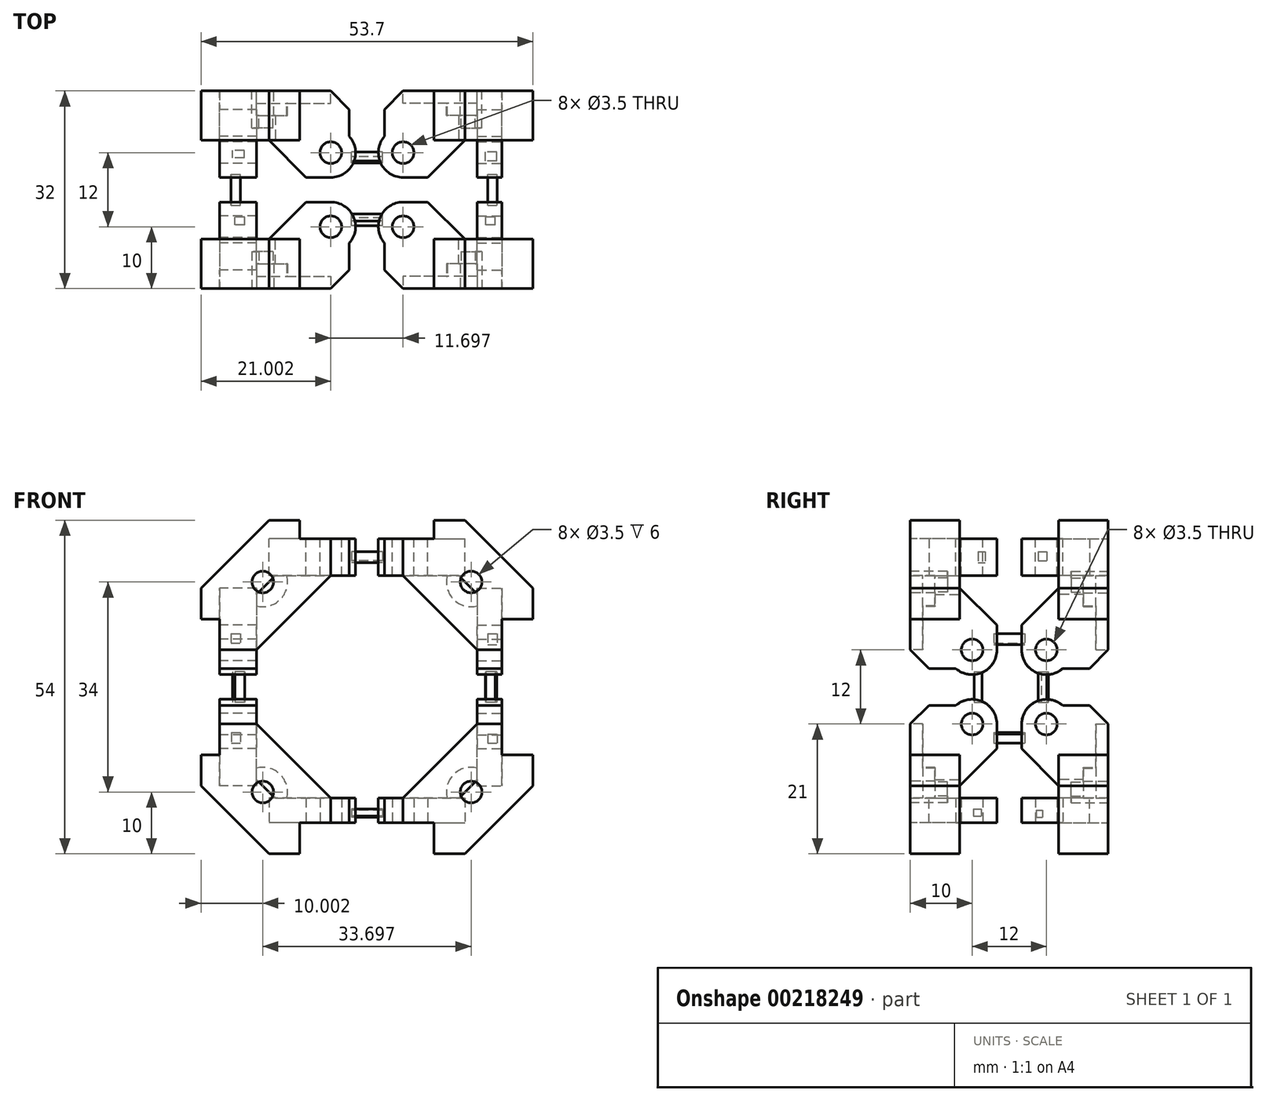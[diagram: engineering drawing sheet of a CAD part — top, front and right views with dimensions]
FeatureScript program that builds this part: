
annotation { "Feature Type Name" : "Feature", "Feature Type Description" : "" }
export const myFeature = defineFeature(function(context is Context, id is Id, definition is map)
    precondition{}
    {
        {
            var Q0;
            Q0=qCreatedBy(makeId("Top.planeOp"),FACE);
            cPlane(context, id + "F0", {"entities" : qUnion([Q0]), "cplaneType" : CPlaneType.OFFSET, "offset" : 18 * mm, "width" : 150 * mm, "height" : 150 * mm});
        }
        {
            var Q0;
            Q0=qCreatedBy(makeId("Front.planeOp"),FACE);
            var sketch = newSketch(context, id + "F1", { "sketchPlane" : qUnion([Q0])});
            skLineSegment(sketch, "E0", {"start": v(14.85, 0) * mm, "end": v(17.85, 0) * mm, "construction": true});
            skLineSegment(sketch, "E1", {"start": v(17.85, 0) * mm, "end": v(17.85, 3) * mm, "construction": true});
            skLineSegment(sketch, "E2", {"start": v(14.85, 0) * mm, "end": v(17.85, 3) * mm});
            skLineSegment(sketch, "E3", {"start": v(14.85, 0) * mm, "end": v(10.85, 0) * mm});
            skLineSegment(sketch, "E4", {"start": v(10.85, 0) * mm, "end": v(10.85, -9) * mm});
            skLineSegment(sketch, "E5", {"start": v(10.85, -9) * mm, "end": v(15.85, -9) * mm});
            skLineSegment(sketch, "E6", {"start": v(17.85, 3) * mm, "end": v(17.85, 7) * mm});
            skLineSegment(sketch, "E7", {"start": v(17.85, 7) * mm, "end": v(26.85, 7) * mm});
            skLineSegment(sketch, "E8", {"start": v(26.85, 7) * mm, "end": v(26.85, 2) * mm});
            skLineSegment(sketch, "E9", {"start": v(26.85, 2) * mm, "end": v(15.85, -9) * mm});
            skLineSegment(sketch, "E10", {"start": v(15.85, -9) * mm, "end": v(26.85, -9) * mm, "construction": true});
            skLineSegment(sketch, "E11", {"start": v(26.85, -9) * mm, "end": v(26.85, 2) * mm, "construction": true});
            skSolve(sketch);
        }
        {
            var Q0;
            Q0=makeQuery(id+"F1.imprint","IMPRINT",FACE,{"disambiguationData":[TD([[makeQuery(id+"F1.imprint","IMPRINT",EDGE,{"derivedFrom":sQuery(id+"F1.wireOp",EDGE,"E2")}),-1.0]])]});
            extrude(context, id + "F2", {"entities" : qUnion([Q0]), "depth" : 8 * mm});
        }
        {
            var Q0;
            Q0=makeQuery(id+"F2.opExtrude","CAP_FACE",FACE,{"disambiguationData":[OSD([sQuery(id+"F1.wireOp",EDGE,"E2"),sQuery(id+"F1.wireOp",EDGE,"E3"),sQuery(id+"F1.wireOp",EDGE,"E4"),sQuery(id+"F1.wireOp",EDGE,"E5"),sQuery(id+"F1.wireOp",EDGE,"E6"),sQuery(id+"F1.wireOp",EDGE,"E7"),sQuery(id+"F1.wireOp",EDGE,"E8"),sQuery(id+"F1.wireOp",EDGE,"E9")])],"isStart":false});
            var sketch = newSketch(context, id + "F3", { "sketchPlane" : qUnion([Q0])});
            skLineSegment(sketch, "E12", {"start": v(26.85, -9) * mm, "end": v(26.85, 2) * mm, "construction": true});
            skLineSegment(sketch, "E13", {"start": v(26.85, 1) * mm, "end": v(16.85, 1) * mm, "construction": true});
            skCircle(sketch, "E14", {"center": v(16.85, 1) * mm, "radius": 1.75 * mm});
            skCircle(sketch, "E15", {"center": v(16.85, 1) * mm, "radius": 4 * mm});
            skLineSegment(sketch, "E16", {"start": v(26.85, -9) * mm, "end": v(15.85, -9) * mm, "construction": true});
            skSolve(sketch);
        }
        {
            var Q0;
            {var subQ0=sQuery(id+"F3.wireOp",EDGE,"xhRyTsUT-o3e5-bvfq-njYf-te9PrhzOYERQ");Q0=makeQuery(id+"F3.imprint","IMPRINT",FACE,{"disambiguationData":[TD([[makeQuery(id+"F3.imprint","IMPRINT",EDGE,{"derivedFrom":subQ0}),-1.0]])]});}
            var Q1;
            Q1=makeQuery(id+"F3.imprint","IMPRINT",FACE,{"disambiguationData":[TD([[makeQuery(id+"F3.imprint","IMPRINT",EDGE,{"derivedFrom":sQuery(id+"F3.wireOp",EDGE,"E14")}),-1.0]])]});
            var Q2;
            {var subQ0=sQuery(id+"F3.wireOp",EDGE,"xAzglln9-Erma-ZddH-ddn6-ssYke3hLXc0D");Q2=makeQuery(id+"F3.imprint","IMPRINT",FACE,{"disambiguationData":[TD([[makeQuery(id+"F3.imprint","IMPRINT",EDGE,{"derivedFrom":subQ0}),1.0]])]});}
            extrude(context, id + "F4", {"entities" : qUnion([Q0, Q1, Q2]), "operationType" : NewBodyOperationType.ADD, "oppositeDirection" : true, "depth" : 4 * mm});
        }
        {
            var Q0;
            Q0=makeQuery(id+"F2.opExtrude","SWEPT_FACE",FACE,{"disambiguationData":[OSD([sQuery(id+"F1.wireOp",EDGE,"E7")])]});
            var sketch = newSketch(context, id + "F5", { "sketchPlane" : qUnion([Q0])});
            skLineSegment(sketch, "E17", {"start": v(21.85, 0) * mm, "end": v(21.85, -8) * mm});
            skLineSegment(sketch, "E18", {"start": v(21.85, 0) * mm, "end": v(17.85, 0) * mm});
            skLineSegment(sketch, "E19", {"start": v(17.85, 0) * mm, "end": v(17.85, -8) * mm});
            skLineSegment(sketch, "E20", {"start": v(17.85, -8) * mm, "end": v(21.85, -8) * mm});
            skSolve(sketch);
        }
        {
            var Q0;
            Q0=makeQuery(id+"F5.imprint","IMPRINT",FACE,{"disambiguationData":[TD([[makeQuery(id+"F5.imprint","IMPRINT",EDGE,{"derivedFrom":sQuery(id+"F5.wireOp",EDGE,"E17")}),-1.0]])]});
            extrude(context, id + "F6", {"entities" : qUnion([Q0]), "operationType" : NewBodyOperationType.ADD, "depth" : 8 * mm});
        }
        {
            var Q0;
            {var subQ0=sQuery(id+"F3.wireOp",EDGE,"E14");var subQ1=makeQuery(id+"F2.opExtrude","CAP_EDGE",EDGE,{"disambiguationData":[OSD([sQuery(id+"F1.wireOp",EDGE,"E2")])],"isStart":false});var subQ2=makeQuery(id+"F3.imprint","INTERSECT",VERTEX,{"disambiguationData":[OD(0.0)],"derivedFrom":[subQ1,subQ0]});Q0=makeQuery(id+"F3.imprint","IMPRINT",FACE,{"disambiguationData":[TD([[makeQuery(id+"F3.imprint","IMPRINT",EDGE,{"disambiguationData":[TD([[subQ2,-1.0]])],"derivedFrom":subQ0}),1.0]])]});}
            extrude(context, id + "F7", {"entities" : qUnion([Q0]), "operationType" : NewBodyOperationType.REMOVE, "oppositeDirection" : true, "depth" : 6 * mm});
        }
        {
            var Q0;
            Q0=makeQuery(id+"F6.opExtrude","SWEPT_FACE",FACE,{"disambiguationData":[OSD([sQuery(id+"F5.wireOp",EDGE,"E17")])]});
            var sketch = newSketch(context, id + "F8", { "sketchPlane" : qUnion([Q0])});
            skLineSegment(sketch, "E21", {"start": v(-8, 12) * mm, "end": v(2, 12) * mm, "construction": true});
            skCircle(sketch, "E22", {"center": v(2, 12) * mm, "radius": 1.75 * mm});
            skCircle(sketch, "E23", {"center": v(2, 12) * mm, "radius": 4 * mm});
            skLineSegment(sketch, "E24", {"start": v(0, 7) * mm, "end": v(0, 2) * mm});
            skLineSegment(sketch, "E25", {"start": v(0, 2) * mm, "end": v(6, 8) * mm});
            skLineSegment(sketch, "E26", {"start": v(2, 12) * mm, "end": v(6, 12) * mm, "construction": true});
            skLineSegment(sketch, "E27", {"start": v(6, 12) * mm, "end": v(6, 8) * mm});
            skSolve(sketch);
        }
        {
            var Q0;
            Q0=qSketchRegion(id+"F8",true);
            var Q1;
            {var subQ0=sQuery(id+"F8.wireOp",EDGE,"GLTiPWO5-g4RS-G08f-K7BW-j4bQh8QSFt7y");Q1=makeQuery(id+"F8.imprint","IMPRINT",FACE,{"disambiguationData":[TD([[makeQuery(id+"F8.imprint","IMPRINT",EDGE,{"derivedFrom":subQ0}),1.0]])]});}
            var Q2;
            {var subQ1=sQuery(id+"F8.wireOp",EDGE,"E24");Q2=makeQuery(id+"F8.imprint","IMPRINT",FACE,{"disambiguationData":[TD([[makeQuery(id+"F8.imprint","IMPRINT",EDGE,{"derivedFrom":subQ1}),1.0]])]});}
            extrude(context, id + "F9", {"entities" : qUnion([Q0, Q1, Q2]), "operationType" : NewBodyOperationType.ADD, "oppositeDirection" : true, "depth" : 4 * mm});
        }
        {
            var Q0;
            Q0=makeQuery(id+"F2.opExtrude","SWEPT_FACE",FACE,{"disambiguationData":[OSD([sQuery(id+"F1.wireOp",EDGE,"E4")])]});
            var sketch = newSketch(context, id + "F10", { "sketchPlane" : qUnion([Q0])});
            skLineSegment(sketch, "E28.bottom", {"start": v(0, 0) * mm, "end": v(8, 0) * mm});
            skLineSegment(sketch, "E28.top", {"start": v(0, -4) * mm, "end": v(8, -4) * mm});
            skLineSegment(sketch, "E28.left", {"start": v(0, 0) * mm, "end": v(0, -4) * mm});
            skLineSegment(sketch, "E28.right", {"start": v(8, 0) * mm, "end": v(8, -4) * mm});
            skSolve(sketch);
        }
        {
            var Q0;
            Q0=makeQuery(id+"F10.imprint","IMPRINT",FACE,{"disambiguationData":[TD([[makeQuery(id+"F10.imprint","IMPRINT",EDGE,{"derivedFrom":sQuery(id+"F10.wireOp",EDGE,"E28.bottom")}),1.0]])]});
            extrude(context, id + "F11", {"entities" : qUnion([Q0]), "operationType" : NewBodyOperationType.ADD, "depth" : 8 * mm});
        }
        {
            var Q0;
            Q0=makeQuery(id+"F11.opExtrude","SWEPT_FACE",FACE,{"disambiguationData":[OSD([sQuery(id+"F10.wireOp",EDGE,"E28.top")])]});
            var sketch = newSketch(context, id + "F12", { "sketchPlane" : qUnion([Q0])});
            skLineSegment(sketch, "E29", {"start": v(5.85, 8) * mm, "end": v(5.85, -2) * mm, "construction": true});
            skCircle(sketch, "E30", {"center": v(5.85, -2) * mm, "radius": 1.75 * mm});
            skCircle(sketch, "E31", {"center": v(5.85, -2) * mm, "radius": 4 * mm});
            skLineSegment(sketch, "E32", {"start": v(10.85, 0) * mm, "end": v(15.85, 0) * mm});
            skLineSegment(sketch, "E33", {"start": v(5.85, -2) * mm, "end": v(5.85, -6) * mm, "construction": true});
            skLineSegment(sketch, "E34", {"start": v(5.85, -6) * mm, "end": v(9.85, -6) * mm});
            skLineSegment(sketch, "E35", {"start": v(9.85, -6) * mm, "end": v(15.85, 0) * mm});
            skSolve(sketch);
        }
        {
            var Q0;
            Q0=makeQuery(id+"F12.imprint","IMPRINT",FACE,{"disambiguationData":[TD([[makeQuery(id+"F12.imprint","IMPRINT",EDGE,{"derivedFrom":sQuery(id+"F12.wireOp",EDGE,"E30")}),-1.0]])]});
            var Q1;
            {var subQ0=sQuery(id+"F12.wireOp",EDGE,"zv0TR8YQ-G6ir-l7lB-xXnJ-DlvVZtNBSlEO");Q1=makeQuery(id+"F12.imprint","IMPRINT",FACE,{"disambiguationData":[TD([[makeQuery(id+"F12.imprint","IMPRINT",EDGE,{"derivedFrom":subQ0}),-1.0]])]});}
            var Q2;
            {var subQ1=sQuery(id+"F12.wireOp",EDGE,"E32");Q2=makeQuery(id+"F12.imprint","IMPRINT",FACE,{"disambiguationData":[TD([[makeQuery(id+"F12.imprint","IMPRINT",EDGE,{"derivedFrom":subQ1}),-1.0]])]});}
            extrude(context, id + "F13", {"entities" : qUnion([Q0, Q1, Q2]), "operationType" : NewBodyOperationType.ADD, "oppositeDirection" : true, "depth" : 4 * mm});
        }
        {
            var Q0;
            Q0=makeQuery(id+"F11.opExtrude","CAP_EDGE",EDGE,{"disambiguationData":[OSD([sQuery(id+"F10.wireOp",EDGE,"E28.right")])],"isStart":false});
            var Q1;
            Q1=makeQuery(id+"F6.opExtrude","CAP_EDGE",EDGE,{"disambiguationData":[OSD([sQuery(id+"F5.wireOp",EDGE,"E20")])],"isStart":false});
            chamfer(context, id + "F14", {"entities" : qUnion([Q0, Q1]), "width" : 3 * mm, "tangentPropagation" : true});
        }
        {
            var Q0;
            Q0=makeQuery(id+"F11.boolean.opBoolean","MERGE",FACE,{"derivedFrom":[makeQuery(id+"F6.boolean.opBoolean","MERGE",FACE,{"derivedFrom":[makeQuery(id+"F4.boolean.opBoolean","MERGE",FACE,{"derivedFrom":[makeQuery(id+"F2.opExtrude","CAP_FACE",FACE,{"disambiguationData":[OSD([sQuery(id+"F1.wireOp",EDGE,"E2"),sQuery(id+"F1.wireOp",EDGE,"E3"),sQuery(id+"F1.wireOp",EDGE,"E4"),sQuery(id+"F1.wireOp",EDGE,"E5"),sQuery(id+"F1.wireOp",EDGE,"E6"),sQuery(id+"F1.wireOp",EDGE,"E7"),sQuery(id+"F1.wireOp",EDGE,"E8"),sQuery(id+"F1.wireOp",EDGE,"E9")])],"isStart":false}),makeQuery(id+"F4.opExtrude","CAP_FACE",FACE,{"disambiguationData":[OSD([sQuery(id+"F3.wireOp",EDGE,"E14"),sQuery(id+"F3.wireOp",EDGE,"E15")])],"isStart":true})]}),makeQuery(id+"F6.opExtrude","SWEPT_FACE",FACE,{"disambiguationData":[OSD([sQuery(id+"F5.wireOp",EDGE,"E20")])]})]}),makeQuery(id+"F11.opExtrude","SWEPT_FACE",FACE,{"disambiguationData":[OSD([sQuery(id+"F10.wireOp",EDGE,"E28.right")])]})]});
            var sketch = newSketch(context, id + "F15", { "sketchPlane" : qUnion([Q0])});
            skLineSegment(sketch, "E36", {"start": v(17.85, 12) * mm, "end": v(5.85, 0) * mm});
            skSolve(sketch);
        }
        {
            var Q0;
            Q0=makeQuery(id+"F15.imprint","IMPRINT",FACE,{"disambiguationData":[TD([[makeQuery(id+"F15.imprint","IMPRINT",EDGE,{"derivedFrom":sQuery(id+"F15.wireOp",EDGE,"E36")}),1.0]])]});
            extrude(context, id + "F16", {"entities" : qUnion([Q0]), "operationType" : NewBodyOperationType.ADD, "oppositeDirection" : true, "depth" : 2 * mm});
        }
        {
            var Q0;
            Q0=makeQuery(id+"F2.opExtrude","SWEPT_BODY",BODY,{"disambiguationData":[OSD([sQuery(id+"F1.wireOp",EDGE,"E2"),sQuery(id+"F1.wireOp",EDGE,"E3"),sQuery(id+"F1.wireOp",EDGE,"E4"),sQuery(id+"F1.wireOp",EDGE,"E5"),sQuery(id+"F1.wireOp",EDGE,"E6"),sQuery(id+"F1.wireOp",EDGE,"E7"),sQuery(id+"F1.wireOp",EDGE,"E8"),sQuery(id+"F1.wireOp",EDGE,"E9")])]});
            var Q1;
            Q1=qCreatedBy(makeId("Right.planeOp"),FACE);
            mirror(context, id + "F17", {"entities" : qUnion([Q0]), "mirrorPlane" : qUnion([Q1])});
        }
        {
            var Q0;
            {var subQ0=sQuery(id+"F5.wireOp",EDGE,"E17");Q0=makeQuery(id+"F17.opPattern","COPY",FACE,{"derivedFrom":makeQuery(id+"F9.boolean.opBoolean","MERGE",FACE,{"derivedFrom":[makeQuery(id+"F6.opExtrude","SWEPT_FACE",FACE,{"disambiguationData":[OSD([subQ0])]}),makeQuery(id+"F9.opExtrude","CAP_FACE",FACE,{"disambiguationData":[OSD([sQuery(id+"F1.wireOp",EDGE,"E7"),subQ0,sQuery(id+"F5.wireOp",EDGE,"E18"),sQuery(id+"F8.wireOp",EDGE,"E22"),sQuery(id+"F8.wireOp",EDGE,"E23"),sQuery(id+"F8.wireOp",EDGE,"E24"),sQuery(id+"F8.wireOp",EDGE,"E25"),sQuery(id+"F8.wireOp",EDGE,"E27")])],"isStart":true})]}),"instanceName":"1"});}
            extrude(context, id + "F18", {"entities" : qUnion([Q0]), "operationType" : NewBodyOperationType.ADD, "depth" : 2 * mm});
        }
        {
            var Q0;
            Q0=makeQuery(id+"F17.opPattern","COPY",BODY,{"derivedFrom":makeQuery(id+"F2.opExtrude","SWEPT_BODY",BODY,{"disambiguationData":[OSD([sQuery(id+"F1.wireOp",EDGE,"E2"),sQuery(id+"F1.wireOp",EDGE,"E3"),sQuery(id+"F1.wireOp",EDGE,"E4"),sQuery(id+"F1.wireOp",EDGE,"E5"),sQuery(id+"F1.wireOp",EDGE,"E6"),sQuery(id+"F1.wireOp",EDGE,"E7"),sQuery(id+"F1.wireOp",EDGE,"E8"),sQuery(id+"F1.wireOp",EDGE,"E9")])]}),"instanceName":"1"});
            var Q1;
            Q1=qCreatedBy(id+"F0.planeOp",FACE);
            mirror(context, id + "F19", {"entities" : qUnion([Q0]), "mirrorPlane" : qUnion([Q1])});
        }
        {
            var Q0;
            {var subQ0=sQuery(id+"F10.wireOp",EDGE,"E28.top");Q0=makeQuery(id+"F19.opPattern","COPY",FACE,{"derivedFrom":makeQuery(id+"F17.opPattern","COPY",FACE,{"derivedFrom":makeQuery(id+"F13.boolean.opBoolean","MERGE",FACE,{"derivedFrom":[makeQuery(id+"F11.opExtrude","SWEPT_FACE",FACE,{"disambiguationData":[OSD([subQ0])]}),makeQuery(id+"F13.opExtrude","CAP_FACE",FACE,{"disambiguationData":[OSD([sQuery(id+"F1.wireOp",EDGE,"E4"),subQ0,sQuery(id+"F10.wireOp",EDGE,"E28.left"),sQuery(id+"F12.wireOp",EDGE,"E30"),sQuery(id+"F12.wireOp",EDGE,"E31"),sQuery(id+"F12.wireOp",EDGE,"E32"),sQuery(id+"F12.wireOp",EDGE,"E34"),sQuery(id+"F12.wireOp",EDGE,"E35")])],"isStart":true})]}),"instanceName":"1"}),"instanceName":"1"});}
            extrude(context, id + "F20", {"entities" : qUnion([Q0]), "operationType" : NewBodyOperationType.ADD, "depth" : 2 * mm});
        }
        {
            var Q0;
            Q0=qCreatedBy(makeId("Front.planeOp"),FACE);
            cPlane(context, id + "F21", {"entities" : qUnion([Q0]), "cplaneType" : CPlaneType.OFFSET, "offset" : 8 * mm, "oppositeDirection" : true, "width" : 150 * mm, "height" : 150 * mm});
        }
        {
            var Q0;
            Q0=makeQuery(id+"F17.opPattern","COPY",BODY,{"derivedFrom":makeQuery(id+"F2.opExtrude","SWEPT_BODY",BODY,{"disambiguationData":[OSD([sQuery(id+"F1.wireOp",EDGE,"E2"),sQuery(id+"F1.wireOp",EDGE,"E3"),sQuery(id+"F1.wireOp",EDGE,"E4"),sQuery(id+"F1.wireOp",EDGE,"E5"),sQuery(id+"F1.wireOp",EDGE,"E6"),sQuery(id+"F1.wireOp",EDGE,"E7"),sQuery(id+"F1.wireOp",EDGE,"E8"),sQuery(id+"F1.wireOp",EDGE,"E9")])]}),"instanceName":"1"});
            var Q1;
            Q1=makeQuery(id+"F19.opPattern","COPY",BODY,{"derivedFrom":makeQuery(id+"F17.opPattern","COPY",BODY,{"derivedFrom":makeQuery(id+"F2.opExtrude","SWEPT_BODY",BODY,{"disambiguationData":[OSD([sQuery(id+"F1.wireOp",EDGE,"E2"),sQuery(id+"F1.wireOp",EDGE,"E3"),sQuery(id+"F1.wireOp",EDGE,"E4"),sQuery(id+"F1.wireOp",EDGE,"E5"),sQuery(id+"F1.wireOp",EDGE,"E6"),sQuery(id+"F1.wireOp",EDGE,"E7"),sQuery(id+"F1.wireOp",EDGE,"E8"),sQuery(id+"F1.wireOp",EDGE,"E9")])]}),"instanceName":"1"}),"instanceName":"1"});
            var Q2;
            Q2=qCreatedBy(id+"F21.planeOp",FACE);
            mirror(context, id + "F22", {"entities" : qUnion([Q0, Q1]), "mirrorPlane" : qUnion([Q2])});
        }
        {
            var Q0;
            Q0=makeQuery(id+"F2.opExtrude","SWEPT_BODY",BODY,{"disambiguationData":[OSD([sQuery(id+"F1.wireOp",EDGE,"E2"),sQuery(id+"F1.wireOp",EDGE,"E3"),sQuery(id+"F1.wireOp",EDGE,"E4"),sQuery(id+"F1.wireOp",EDGE,"E5"),sQuery(id+"F1.wireOp",EDGE,"E6"),sQuery(id+"F1.wireOp",EDGE,"E7"),sQuery(id+"F1.wireOp",EDGE,"E8"),sQuery(id+"F1.wireOp",EDGE,"E9")])]});
            var Q1;
            Q1=qCreatedBy(id+"F21.planeOp",FACE);
            mirror(context, id + "F23", {"entities" : qUnion([Q0]), "mirrorPlane" : qUnion([Q1])});
        }
        {
            var Q0;
            Q0=makeQuery(id+"F2.opExtrude","SWEPT_BODY",BODY,{"disambiguationData":[OSD([sQuery(id+"F1.wireOp",EDGE,"E2"),sQuery(id+"F1.wireOp",EDGE,"E3"),sQuery(id+"F1.wireOp",EDGE,"E4"),sQuery(id+"F1.wireOp",EDGE,"E5"),sQuery(id+"F1.wireOp",EDGE,"E6"),sQuery(id+"F1.wireOp",EDGE,"E7"),sQuery(id+"F1.wireOp",EDGE,"E8"),sQuery(id+"F1.wireOp",EDGE,"E9")])]});
            var Q1;
            Q1=makeQuery(id+"F23.opPattern","COPY",BODY,{"derivedFrom":makeQuery(id+"F2.opExtrude","SWEPT_BODY",BODY,{"disambiguationData":[OSD([sQuery(id+"F1.wireOp",EDGE,"E2"),sQuery(id+"F1.wireOp",EDGE,"E3"),sQuery(id+"F1.wireOp",EDGE,"E4"),sQuery(id+"F1.wireOp",EDGE,"E5"),sQuery(id+"F1.wireOp",EDGE,"E6"),sQuery(id+"F1.wireOp",EDGE,"E7"),sQuery(id+"F1.wireOp",EDGE,"E8"),sQuery(id+"F1.wireOp",EDGE,"E9")])]}),"instanceName":"1"});
            var Q2;
            Q2=qCreatedBy(id+"F0.planeOp",FACE);
            mirror(context, id + "F24", {"entities" : qUnion([Q0, Q1]), "mirrorPlane" : qUnion([Q2])});
        }
        {
            var Q0;
            {var subQ0=sQuery(id+"F10.wireOp",EDGE,"E28.top");Q0=makeQuery(id+"F24.opPattern","COPY",FACE,{"derivedFrom":makeQuery(id+"F13.boolean.opBoolean","MERGE",FACE,{"derivedFrom":[makeQuery(id+"F11.opExtrude","SWEPT_FACE",FACE,{"disambiguationData":[OSD([subQ0])]}),makeQuery(id+"F13.opExtrude","CAP_FACE",FACE,{"disambiguationData":[OSD([sQuery(id+"F1.wireOp",EDGE,"E4"),subQ0,sQuery(id+"F10.wireOp",EDGE,"E28.left"),sQuery(id+"F12.wireOp",EDGE,"E30"),sQuery(id+"F12.wireOp",EDGE,"E31"),sQuery(id+"F12.wireOp",EDGE,"E32"),sQuery(id+"F12.wireOp",EDGE,"E34"),sQuery(id+"F12.wireOp",EDGE,"E35")])],"isStart":true})]}),"instanceName":"1"});}
            var Q1;
            {var subQ0=sQuery(id+"F10.wireOp",EDGE,"E28.top");Q1=makeQuery(id+"F24.opPattern","COPY",FACE,{"derivedFrom":makeQuery(id+"F23.opPattern","COPY",FACE,{"derivedFrom":makeQuery(id+"F13.boolean.opBoolean","MERGE",FACE,{"derivedFrom":[makeQuery(id+"F11.opExtrude","SWEPT_FACE",FACE,{"disambiguationData":[OSD([subQ0])]}),makeQuery(id+"F13.opExtrude","CAP_FACE",FACE,{"disambiguationData":[OSD([sQuery(id+"F1.wireOp",EDGE,"E4"),subQ0,sQuery(id+"F10.wireOp",EDGE,"E28.left"),sQuery(id+"F12.wireOp",EDGE,"E30"),sQuery(id+"F12.wireOp",EDGE,"E31"),sQuery(id+"F12.wireOp",EDGE,"E32"),sQuery(id+"F12.wireOp",EDGE,"E34"),sQuery(id+"F12.wireOp",EDGE,"E35")])],"isStart":true})]}),"instanceName":"1"}),"instanceName":"1"});}
            extrude(context, id + "F25", {"entities" : qUnion([Q0, Q1]), "operationType" : NewBodyOperationType.ADD, "depth" : 2 * mm});
        }
        {
            var Q0;
            Q0=qCreatedBy(id+"F21.planeOp",FACE);
            var sketch = newSketch(context, id + "F26", { "sketchPlane" : qUnion([Q0])});
            skLineSegment(sketch, "E37.bottom", {"start": v(-22.03, 26.65) * mm, "end": v(-20.49, 26.65) * mm});
            skLineSegment(sketch, "E37.top", {"start": v(-22.03, 25.11) * mm, "end": v(-20.49, 25.11) * mm});
            skLineSegment(sketch, "E37.left", {"start": v(-22.03, 26.65) * mm, "end": v(-22.03, 25.11) * mm});
            skLineSegment(sketch, "E37.right", {"start": v(-20.49, 26.65) * mm, "end": v(-20.49, 25.11) * mm});
            skLineSegment(sketch, "E38.bottom", {"start": v(-21.94, 10.62) * mm, "end": v(-20.49, 10.62) * mm});
            skLineSegment(sketch, "E38.top", {"start": v(-21.94, 8.92) * mm, "end": v(-20.49, 8.92) * mm});
            skLineSegment(sketch, "E38.left", {"start": v(-21.94, 10.62) * mm, "end": v(-21.94, 8.92) * mm});
            skLineSegment(sketch, "E38.right", {"start": v(-20.49, 10.62) * mm, "end": v(-20.49, 8.92) * mm});
            skLineSegment(sketch, "E39.bottom", {"start": v(19.51, 10.38) * mm, "end": v(21.05, 10.38) * mm});
            skLineSegment(sketch, "E39.top", {"start": v(19.51, 8.92) * mm, "end": v(21.05, 8.92) * mm});
            skLineSegment(sketch, "E39.left", {"start": v(19.51, 10.38) * mm, "end": v(19.51, 8.92) * mm});
            skLineSegment(sketch, "E39.right", {"start": v(21.05, 10.38) * mm, "end": v(21.05, 8.92) * mm});
            skLineSegment(sketch, "E40.bottom", {"start": v(19.51, 26.65) * mm, "end": v(21.05, 26.65) * mm});
            skLineSegment(sketch, "E40.top", {"start": v(19.51, 24.87) * mm, "end": v(21.05, 24.87) * mm});
            skLineSegment(sketch, "E40.left", {"start": v(19.51, 26.65) * mm, "end": v(19.51, 24.87) * mm});
            skLineSegment(sketch, "E40.right", {"start": v(21.05, 26.65) * mm, "end": v(21.05, 24.87) * mm});
            skLineSegment(sketch, "E41", {"start": v(-20.49, 26.65) * mm, "end": v(19.51, 26.65) * mm, "construction": true});
            skLineSegment(sketch, "E42", {"start": v(-20.49, 8.92) * mm, "end": v(19.51, 8.92) * mm, "construction": true});
            skSolve(sketch);
        }
        {
            var Q0;
            Q0=qSketchRegion(id+"F26",true);
            extrude(context, id + "F27", {"entities" : qUnion([Q0]), "endBound" : BoundingType.SYMMETRIC, "depth" : 5 * mm});
        }
        {
            var Q0;
            Q0=qCreatedBy(id+"F0.planeOp",FACE);
            var sketch = newSketch(context, id + "F28", { "sketchPlane" : qUnion([Q0])});
            skLineSegment(sketch, "E43.bottom", {"start": v(20.73, 2.3) * mm, "end": v(19.21, 2.3) * mm});
            skLineSegment(sketch, "E43.top", {"start": v(20.73, 3.57) * mm, "end": v(19.21, 3.57) * mm});
            skLineSegment(sketch, "E43.left", {"start": v(20.73, 2.3) * mm, "end": v(20.73, 3.57) * mm});
            skLineSegment(sketch, "E43.right", {"start": v(19.21, 2.3) * mm, "end": v(19.21, 3.57) * mm});
            skLineSegment(sketch, "E44.bottom", {"start": v(-19.78, 2.3) * mm, "end": v(-21.38, 2.3) * mm});
            skLineSegment(sketch, "E44.top", {"start": v(-19.78, 3.57) * mm, "end": v(-21.38, 3.57) * mm});
            skLineSegment(sketch, "E44.left", {"start": v(-19.78, 2.3) * mm, "end": v(-19.78, 3.57) * mm});
            skLineSegment(sketch, "E44.right", {"start": v(-21.38, 2.3) * mm, "end": v(-21.38, 3.57) * mm});
            skLineSegment(sketch, "E45.bottom", {"start": v(-19.86, 13.17) * mm, "end": v(-21.72, 13.17) * mm});
            skLineSegment(sketch, "E45.top", {"start": v(-19.86, 14.35) * mm, "end": v(-21.72, 14.35) * mm});
            skLineSegment(sketch, "E45.left", {"start": v(-19.86, 13.17) * mm, "end": v(-19.86, 14.35) * mm});
            skLineSegment(sketch, "E45.right", {"start": v(-21.72, 13.17) * mm, "end": v(-21.72, 14.35) * mm});
            skLineSegment(sketch, "E46.bottom", {"start": v(20.98, 12.67) * mm, "end": v(19.13, 12.67) * mm});
            skLineSegment(sketch, "E46.top", {"start": v(20.98, 14.1) * mm, "end": v(19.13, 14.1) * mm});
            skLineSegment(sketch, "E46.left", {"start": v(20.98, 12.67) * mm, "end": v(20.98, 14.1) * mm});
            skLineSegment(sketch, "E46.right", {"start": v(19.13, 12.67) * mm, "end": v(19.13, 14.1) * mm});
            skSolve(sketch);
        }
        {
            var Q0;
            Q0=qSketchRegion(id+"F28",true);
            extrude(context, id + "F29", {"entities" : qUnion([Q0]), "endBound" : BoundingType.SYMMETRIC, "depth" : 5 * mm});
        }
        {
            var Q0;
            Q0=qCreatedBy(makeId("Right.planeOp"),FACE);
            var sketch = newSketch(context, id + "F30", { "sketchPlane" : qUnion([Q0])});
            skLineSegment(sketch, "E47.bottom", {"start": v(2.96, 39.89) * mm, "end": v(4.08, 39.89) * mm});
            skLineSegment(sketch, "E47.top", {"start": v(2.96, 38.14) * mm, "end": v(4.08, 38.14) * mm});
            skLineSegment(sketch, "E47.left", {"start": v(2.96, 39.89) * mm, "end": v(2.96, 38.14) * mm});
            skLineSegment(sketch, "E47.right", {"start": v(4.08, 39.89) * mm, "end": v(4.08, 38.14) * mm});
            skLineSegment(sketch, "E48.bottom", {"start": v(12.66, 39.89) * mm, "end": v(14.1, 39.89) * mm});
            skLineSegment(sketch, "E48.top", {"start": v(12.66, 38.46) * mm, "end": v(14.1, 38.46) * mm});
            skLineSegment(sketch, "E48.left", {"start": v(12.66, 39.89) * mm, "end": v(12.66, 38.46) * mm});
            skLineSegment(sketch, "E48.right", {"start": v(14.1, 39.89) * mm, "end": v(14.1, 38.46) * mm});
            skLineSegment(sketch, "E49.bottom", {"start": v(2.17, -1.76) * mm, "end": v(3.44, -1.76) * mm});
            skLineSegment(sketch, "E49.top", {"start": v(2.17, -2.88) * mm, "end": v(3.44, -2.88) * mm});
            skLineSegment(sketch, "E49.left", {"start": v(2.17, -1.76) * mm, "end": v(2.17, -2.88) * mm});
            skLineSegment(sketch, "E49.right", {"start": v(3.44, -1.76) * mm, "end": v(3.44, -2.88) * mm});
            skLineSegment(sketch, "E50.bottom", {"start": v(12.34, -1.92) * mm, "end": v(13.37, -1.92) * mm});
            skLineSegment(sketch, "E50.top", {"start": v(12.34, -3.11) * mm, "end": v(13.37, -3.11) * mm});
            skLineSegment(sketch, "E50.left", {"start": v(12.34, -1.92) * mm, "end": v(12.34, -3.11) * mm});
            skLineSegment(sketch, "E50.right", {"start": v(13.37, -1.92) * mm, "end": v(13.37, -3.11) * mm});
            skSolve(sketch);
        }
        {
            var Q0;
            Q0=qSketchRegion(id+"F30",true);
            extrude(context, id + "F31", {"entities" : qUnion([Q0]), "endBound" : BoundingType.SYMMETRIC, "depth" : 5 * mm});
        }
    });
